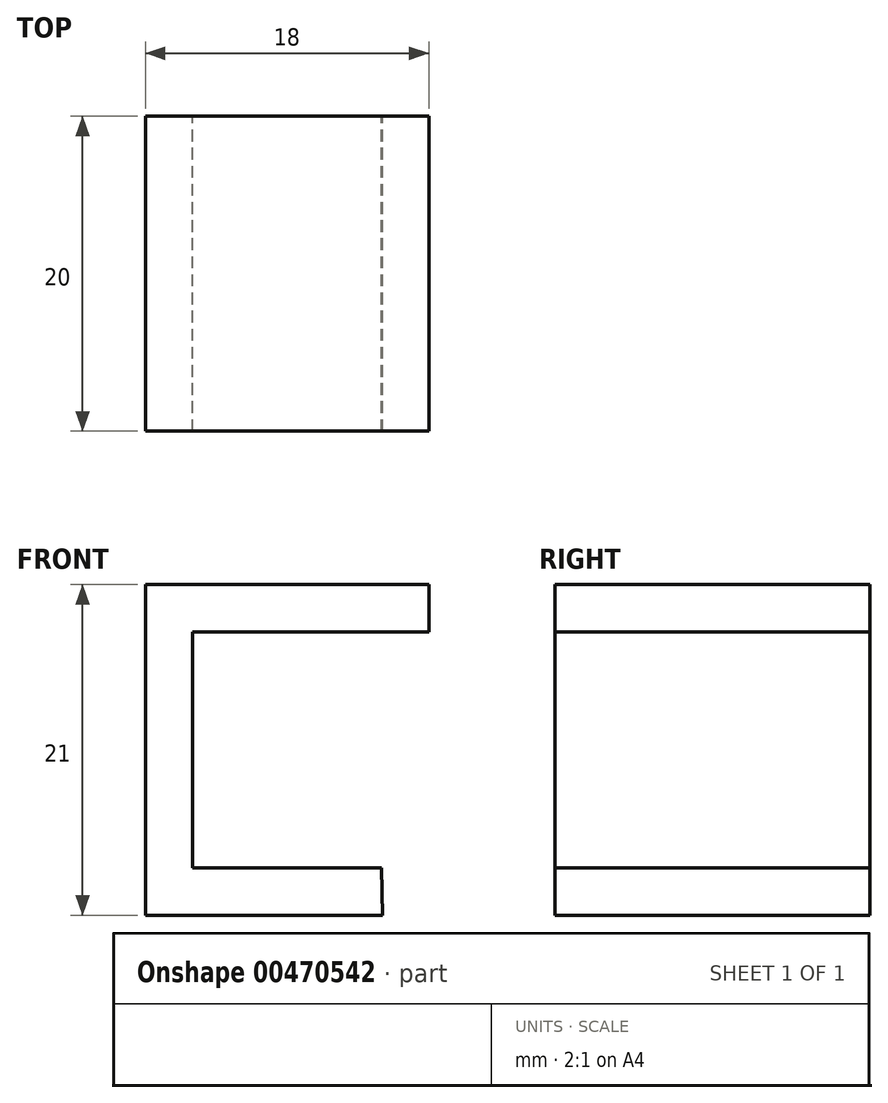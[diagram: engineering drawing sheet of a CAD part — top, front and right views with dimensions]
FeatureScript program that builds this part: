
annotation { "Feature Type Name" : "Feature", "Feature Type Description" : "" }
export const myFeature = defineFeature(function(context is Context, id is Id, definition is map)
    precondition{}
    {
        {
            var Q0;
            Q0=qCreatedBy(makeId("Front.planeOp"),FACE);
            var sketch = newSketch(context, id + "F0", { "sketchPlane" : qUnion([Q0])});
            skLineSegment(sketch, "E0", {"start": v(1.35, 11.3) * mm, "end": v(-13.65, 11.3) * mm});
            skLineSegment(sketch, "E1", {"start": v(-13.65, 11.3) * mm, "end": v(-13.65, -3.7) * mm});
            skLineSegment(sketch, "E2", {"start": v(-13.65, -3.7) * mm, "end": v(-1.65, -3.7) * mm});
            skLineSegment(sketch, "E3.0", {"start": v(-16.65, -6.7) * mm, "end": v(-1.6, -6.7) * mm});
            skLineSegment(sketch, "E3.1", {"start": v(-16.65, 14.3) * mm, "end": v(-16.65, -6.7) * mm});
            skLineSegment(sketch, "E3.2", {"start": v(1.35, 14.3) * mm, "end": v(-16.65, 14.3) * mm});
            skLineSegment(sketch, "E4", {"start": v(-1.6, -6.7) * mm, "end": v(-1.65, -3.7) * mm});
            skLineSegment(sketch, "E5", {"start": v(1.35, 11.3) * mm, "end": v(1.35, 14.3) * mm});
            skSolve(sketch);
        }
        {
            var Q0;
            Q0 = qSketchRegion(id + "F0", true);
            extrude(context, id + "F1", {"entities" : qUnion([Q0]), "endBound" : BoundingType.SYMMETRIC, "depth" : 20 * mm});
        }
    });
